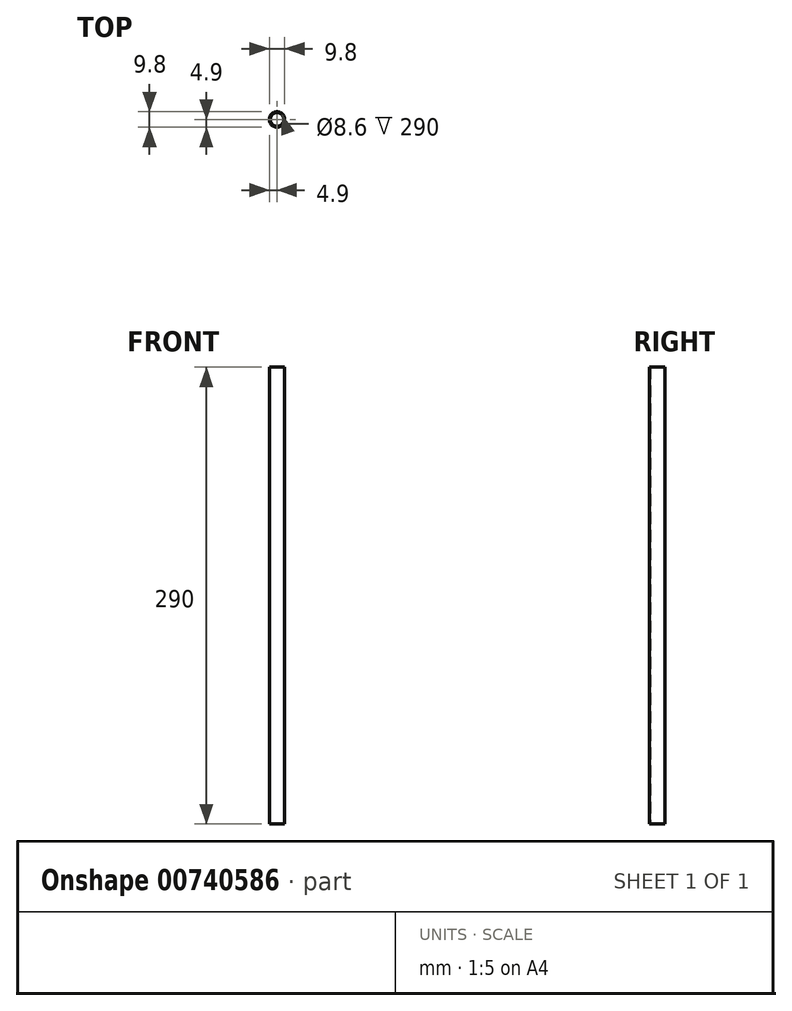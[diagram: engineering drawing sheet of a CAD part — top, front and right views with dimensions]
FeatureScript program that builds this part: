
annotation { "Feature Type Name" : "Feature", "Feature Type Description" : "" }
export const myFeature = defineFeature(function(context is Context, id is Id, definition is map)
    precondition{}
    {
        {
            var Q0;
            Q0=qCreatedBy(makeId("Top.planeOp"),FACE);
            var sketch = newSketch(context, id + "F0", { "sketchPlane" : qUnion([Q0])});
            skCircle(sketch, "E0", {"center": v(0, 0) * mm, "radius": 4.9 * mm});
            skCircle(sketch, "E1", {"center": v(0, 0) * mm, "radius": 4.3 * mm});
            skSolve(sketch);
        }
        {
            var Q0;
            Q0=makeQuery(id+"F0.imprint","IMPRINT",FACE,{"disambiguationData":[TD([[makeQuery(id+"F0.imprint","IMPRINT",EDGE,{"derivedFrom":sQuery(id+"F0.wireOp",EDGE,"E0")}),1.0]])]});
            extrude(context, id + "F1", {"entities" : qUnion([Q0]), "depth" : (153 + 137) * mm, "offsetDistance" : 25 * mm});
        }
    });
